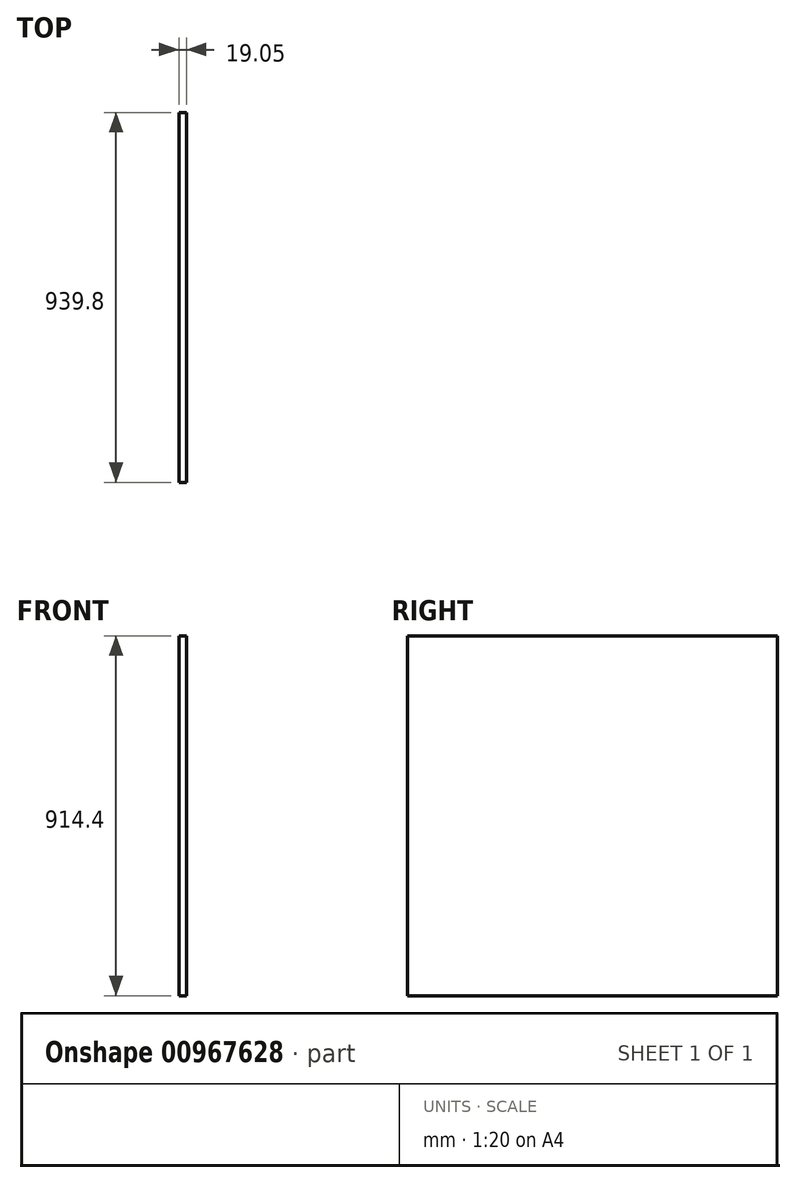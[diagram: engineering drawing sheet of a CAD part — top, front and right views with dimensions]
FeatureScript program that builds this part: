
annotation { "Feature Type Name" : "Feature", "Feature Type Description" : "" }
export const myFeature = defineFeature(function(context is Context, id is Id, definition is map)
    precondition{}
    {
        {
            var Q0;
            Q0=qCreatedBy(makeId("Right.planeOp"),FACE);
            var sketch = newSketch(context, id + "F0", { "sketchPlane" : qUnion([Q0])});
            skLineSegment(sketch, "E0.bottom", {"start": v(469.9, 457.2) * mm, "end": v(-469.9, 457.2) * mm});
            skLineSegment(sketch, "E0.top", {"start": v(469.9, -457.2) * mm, "end": v(-469.9, -457.2) * mm});
            skLineSegment(sketch, "E0.left", {"start": v(469.9, 457.2) * mm, "end": v(469.9, -457.2) * mm});
            skLineSegment(sketch, "E0.right", {"start": v(-469.9, 457.2) * mm, "end": v(-469.9, -457.2) * mm});
            skPoint(sketch, "E0.middle", {"position": v(0, 0) * mm});
            skSolve(sketch);
        }
        {
            var Q0;
            Q0 = qSketchRegion(id + "F0", true);
            extrude(context, id + "F1", {"entities" : qUnion([Q0]), "depth" : 19.05 * mm, "offsetDistance" : 25.4 * mm});
        }
    });
